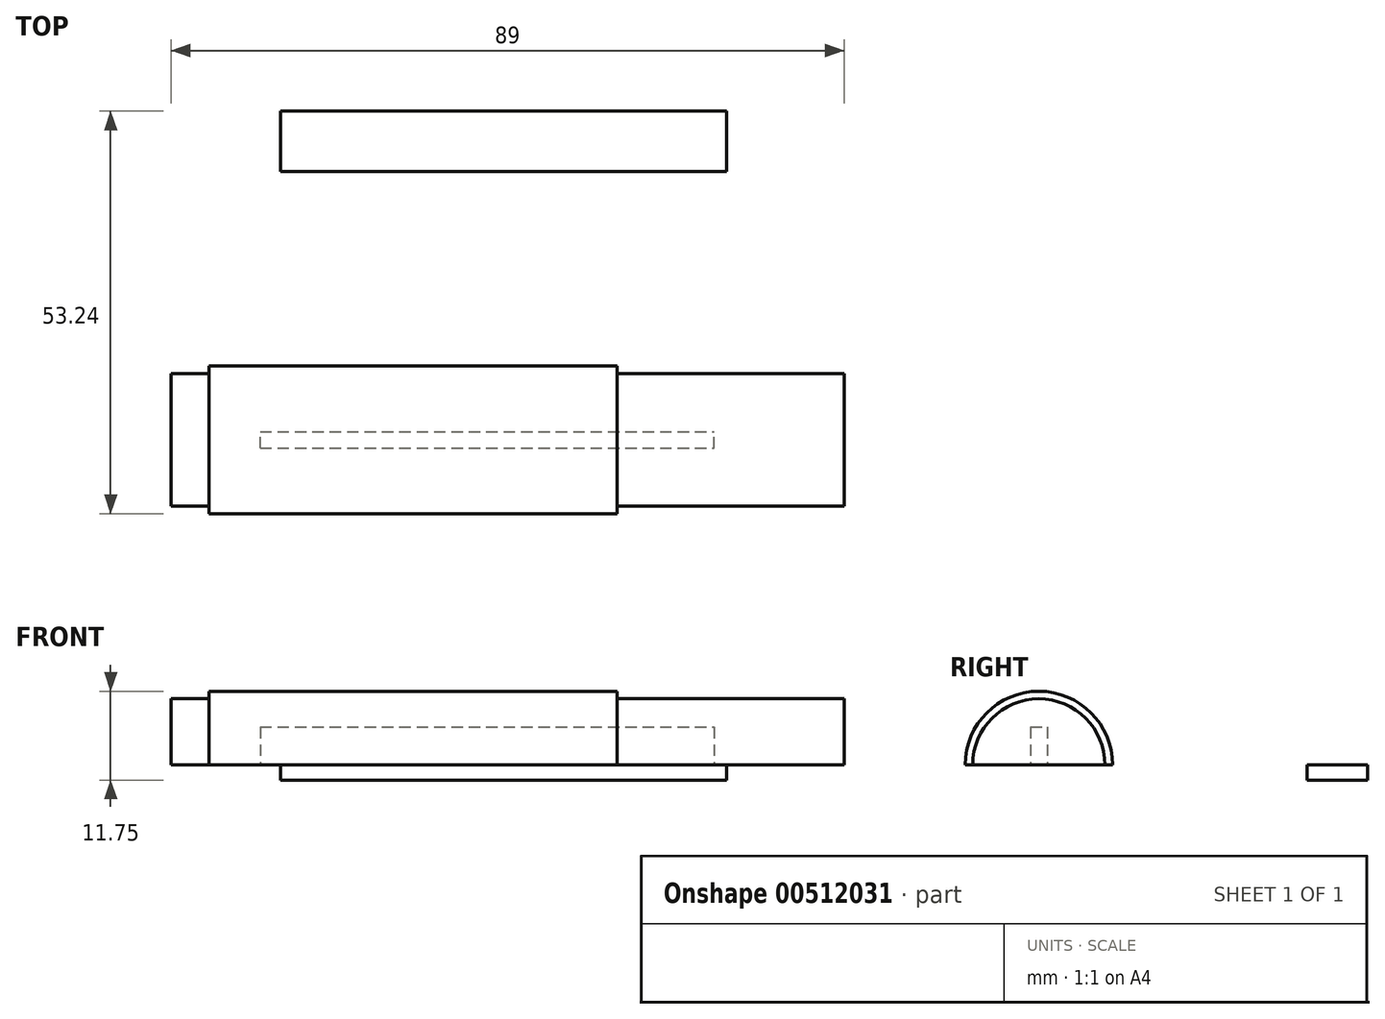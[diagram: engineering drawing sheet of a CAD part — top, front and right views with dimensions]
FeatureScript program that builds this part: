
annotation { "Feature Type Name" : "Feature", "Feature Type Description" : "" }
export const myFeature = defineFeature(function(context is Context, id is Id, definition is map)
    precondition{}
    {
        {
            var Q0;
            Q0=qCreatedBy(makeId("Top.planeOp"),FACE);
            var sketch = newSketch(context, id + "F0", { "sketchPlane" : qUnion([Q0])});
            skLineSegment(sketch, "E0.bottom", {"start": v(-36.77, 0) * mm, "end": v(17.23, 0) * mm});
            skLineSegment(sketch, "E0.top", {"start": v(-36.77, 9.75) * mm, "end": v(17.23, 9.75) * mm});
            skLineSegment(sketch, "E0.left", {"start": v(-36.77, 0) * mm, "end": v(-36.77, 9.75) * mm});
            skLineSegment(sketch, "E0.right", {"start": v(17.23, 0) * mm, "end": v(17.23, 9.75) * mm});
            skLineSegment(sketch, "E1.bottom", {"start": v(-41.77, 0) * mm, "end": v(-36.77, 0) * mm});
            skLineSegment(sketch, "E1.top", {"start": v(-41.77, 8.75) * mm, "end": v(-36.77, 8.75) * mm});
            skLineSegment(sketch, "E1.left", {"start": v(-41.77, 0) * mm, "end": v(-41.77, 8.75) * mm});
            skLineSegment(sketch, "E1.right", {"start": v(-36.77, 0) * mm, "end": v(-36.77, 8.75) * mm});
            skLineSegment(sketch, "E2.bottom", {"start": v(17.23, 8.75) * mm, "end": v(47.23, 8.75) * mm});
            skLineSegment(sketch, "E2.top", {"start": v(17.23, 0) * mm, "end": v(47.23, 0) * mm});
            skLineSegment(sketch, "E2.left", {"start": v(17.23, 8.75) * mm, "end": v(17.23, 0) * mm});
            skLineSegment(sketch, "E2.right", {"start": v(47.23, 8.75) * mm, "end": v(47.23, 0) * mm});
            skSolve(sketch);
        }
        {
            var Q0;
            Q0=makeQuery(id+"F0.imprint","IMPRINT",FACE,{"disambiguationData":[TD([[makeQuery(id+"F0.imprint","IMPRINT",EDGE,{"derivedFrom":sQuery(id+"F0.wireOp",EDGE,"E1.bottom")}),1.0]])]});
            var Q1;
            Q1=makeQuery(id+"F0.imprint","IMPRINT",FACE,{"disambiguationData":[TD([[makeQuery(id+"F0.imprint","IMPRINT",EDGE,{"derivedFrom":sQuery(id+"F0.wireOp",EDGE,"E0.bottom")}),1.0]])]});
            var Q2;
            Q2=makeQuery(id+"F0.imprint","IMPRINT",FACE,{"disambiguationData":[TD([[makeQuery(id+"F0.imprint","IMPRINT",EDGE,{"derivedFrom":sQuery(id+"F0.wireOp",EDGE,"E2.bottom")}),-1.0]])]});
            var Q3;
            Q3=sQuery(id+"F0.wireOp",EDGE,"E0.bottom");
            revolve(context, id + "F1", {"entities" : qUnion([Q0, Q1, Q2]), "axis" : qUnion([Q3]), "revolveType" : RevolveType.ONE_DIRECTION, "angle" : 180 * degree});
        }
        {
            var Q0;
            Q0=makeQuery(id+"F1.opRevolve","CAP_FACE",FACE,{"disambiguationData":[OSD([sQuery(id+"F0.wireOp",EDGE,"E0.bottom"),sQuery(id+"F0.wireOp",EDGE,"E0.top"),sQuery(id+"F0.wireOp",EDGE,"E0.left"),sQuery(id+"F0.wireOp",EDGE,"E0.right"),sQuery(id+"F0.wireOp",EDGE,"E1.bottom"),sQuery(id+"F0.wireOp",EDGE,"E1.top"),sQuery(id+"F0.wireOp",EDGE,"E1.left"),sQuery(id+"F0.wireOp",EDGE,"E2.bottom"),sQuery(id+"F0.wireOp",EDGE,"E2.top"),sQuery(id+"F0.wireOp",EDGE,"E2.right")])],"isStart":false});
            var sketch = newSketch(context, id + "F2", { "sketchPlane" : qUnion([Q0])});
            skLineSegment(sketch, "E3.bottom", {"start": v(-30, 1.1) * mm, "end": v(30, 1.1) * mm});
            skLineSegment(sketch, "E3.top", {"start": v(-30, -1.1) * mm, "end": v(30, -1.1) * mm});
            skLineSegment(sketch, "E3.left", {"start": v(-30, 1.1) * mm, "end": v(-30, -1.1) * mm});
            skLineSegment(sketch, "E3.right", {"start": v(30, 1.1) * mm, "end": v(30, -1.1) * mm});
            skPoint(sketch, "E3.middle", {"position": v(0, 0) * mm});
            skLineSegment(sketch, "E4.bottom", {"start": v(31.66, -43.49) * mm, "end": v(-27.34, -43.49) * mm});
            skLineSegment(sketch, "E4.top", {"start": v(31.66, -35.49) * mm, "end": v(-27.34, -35.49) * mm});
            skLineSegment(sketch, "E4.left", {"start": v(31.66, -43.49) * mm, "end": v(31.66, -35.49) * mm});
            skLineSegment(sketch, "E4.right", {"start": v(-27.34, -43.49) * mm, "end": v(-27.34, -35.49) * mm});
            skPoint(sketch, "E4.middle", {"position": v(2.16, -39.49) * mm});
            skSolve(sketch);
        }
        {
            var Q0;
            Q0=makeQuery(id+"F2.imprint","IMPRINT",FACE,{"disambiguationData":[TD([[makeQuery(id+"F2.imprint","IMPRINT",EDGE,{"derivedFrom":sQuery(id+"F2.wireOp",EDGE,"E3.bottom")}),-1.0]])]});
            extrude(context, id + "F3", {"entities" : qUnion([Q0]), "operationType" : NewBodyOperationType.REMOVE, "oppositeDirection" : true, "depth" : 5 * mm, "offsetDistance" : 25 * mm});
        }
        {
            var Q0;
            Q0=makeQuery(id+"F2.imprint","IMPRINT",FACE,{"disambiguationData":[TD([[makeQuery(id+"F2.imprint","IMPRINT",EDGE,{"derivedFrom":sQuery(id+"F2.wireOp",EDGE,"E4.bottom")}),-1.0]])]});
            extrude(context, id + "F4", {"entities" : qUnion([Q0]), "depth" : 2 * mm, "offsetDistance" : 25 * mm});
        }
    });
